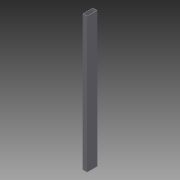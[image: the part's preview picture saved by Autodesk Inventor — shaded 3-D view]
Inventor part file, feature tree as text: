
AUTODESK INVENTOR PART (.ipt)
format: ipt  version: 2014 (Build 180170000, 170)  size: 87,040 bytes
history: native  units: in
note: dims shown in document units (in); Inventor stores cm internally (conversion verified against a paired STEP export)
features: other x4, extrude x1, sketch x1
ambient origin geometry x8: Origin, YZ Plane, XZ Plane, XY Plane, X Axis, Y Axis, Z Axis, Center Point
bodies: Solid1 (feature_tree)
feature tree (6):
  other  "Table"
  other  "squareTube1.75x4.ipt"
  extrude  "Extrusion1"  TaperAngle=0.0deg  [1 undecoded]
  other  "Solid1::squareTube1.75x4.ipt"
  other  "TaggingFeature1"
  sketch  "Sketch1"  dims[d0=1.75in d1=4.0in d2=0.125in d4=0.0in d3=1.0in d5=2.0in d6=0.0in]
note: 1 required parameter value undecoded (feature->parameter linkage not recoverable at this tier; creation-order binding heuristic only, values carry confidence <= 0.55)
